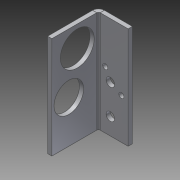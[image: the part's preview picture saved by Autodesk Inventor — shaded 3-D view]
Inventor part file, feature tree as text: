
AUTODESK INVENTOR PART (.ipt)
format: ipt  version: 2014 SP1 (Build 180222100, 222)  size: 156,672 bytes
history: native  units: in
note: dims shown in document units (in); Inventor stores cm internally (conversion verified against a paired STEP export)
features: sheet_metal_op x4, sketch x4, other x4, reference x1
ambient origin geometry x8: Origin, YZ Plane, XZ Plane, XY Plane, X Axis, Y Axis, Z Axis, Center Point
bodies: Solid1 (feature_tree)
feature tree (13):
  sheet_metal_op  "Face1"
  sheet_metal_op  "Flange1"
  sketch  "Sketch1"  dims[d0=1.0in]
  other  "Plate1"
  sketch  "Sketch2"  dims[d1=3.0in]
  other  "Plate2"
  sheet_metal_op  "Bend1"
  sheet_metal_op  "Corner1"
  sketch  "Sketch3"  dims[d2=0.125in]
  sketch  "Sketch4"  dims[d3=0.125in d4=0.0625in d5=0.25in d6=0.125in d7=1.5in d8=90.0deg d9=0.05in d10=0.5in d11=0.125in d12=0.125in d13=1.0in d14=0.875in d15=0.625in d16=0.75in d17=0.5in d18=1.25in d19=0.125in d20=0.0in d21=0.15in d22=0.2in d23=0.2in d24=0.5in d25=0.15in d26=0.125in d27=0.0in d28=0.3in d29=0.25in d30=0.5in d31=0.875in]
  reference  "Reference1"
  other  "Cut1"
  other  "Cut2"
